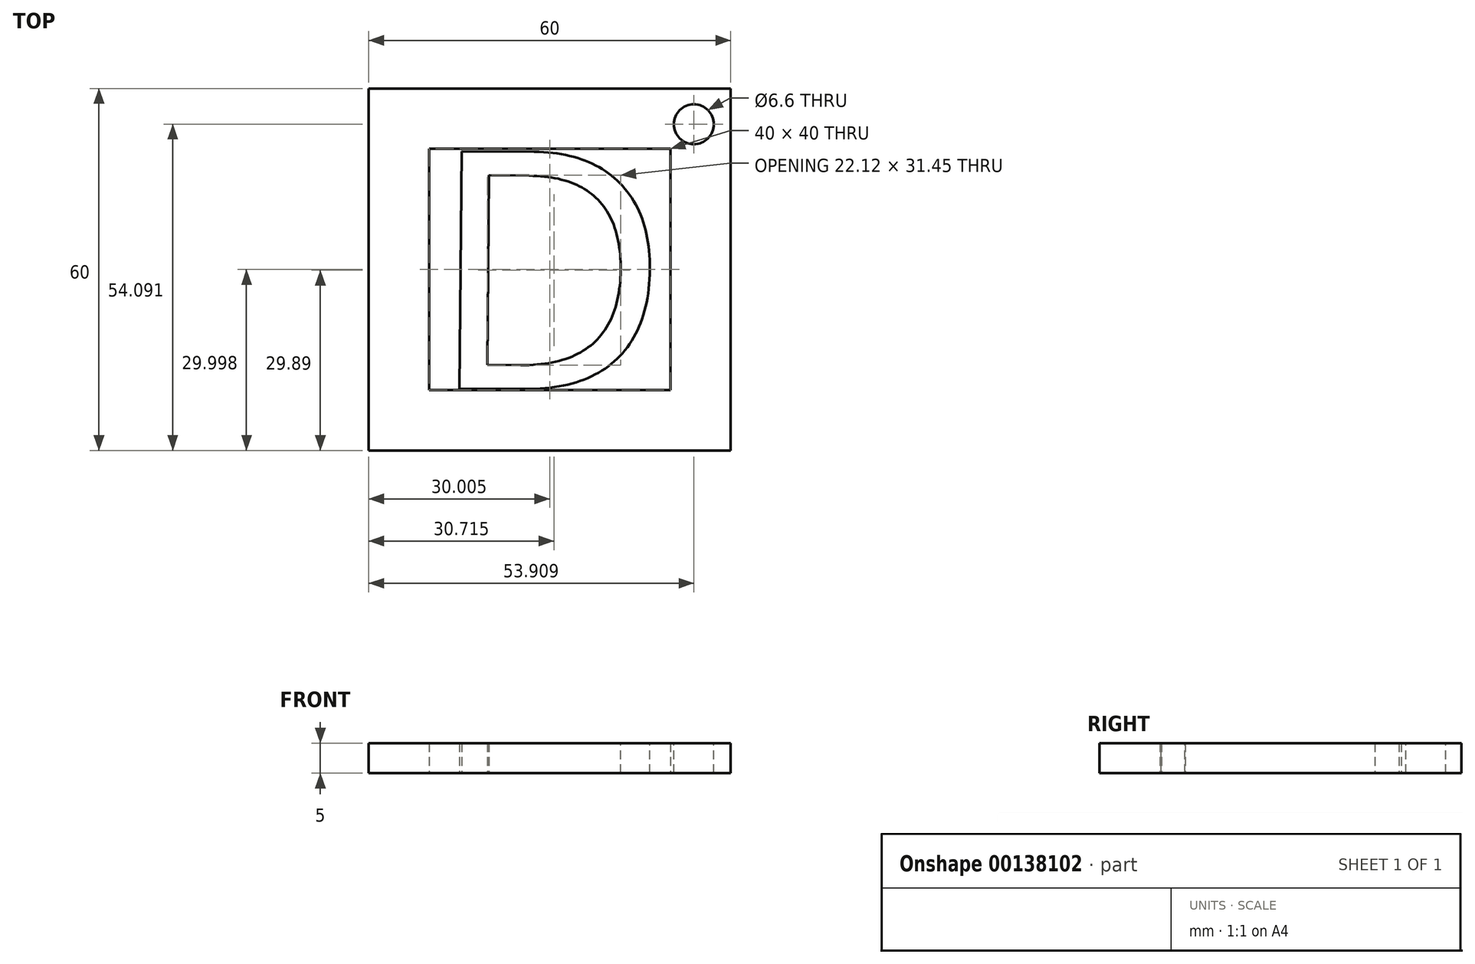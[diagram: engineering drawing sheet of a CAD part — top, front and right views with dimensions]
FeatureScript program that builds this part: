
annotation { "Feature Type Name" : "Feature", "Feature Type Description" : "" }
export const myFeature = defineFeature(function(context is Context, id is Id, definition is map)
    precondition{}
    {
        {
            var Q0;
            Q0=qCreatedBy(makeId("Top.planeOp"),FACE);
            var sketch = newSketch(context, id + "F0", { "sketchPlane" : qUnion([Q0])});
            skLineSegment(sketch, "E0.bottom", {"start": v(-26.05, 20.19) * mm, "end": v(13.95, 20.19) * mm});
            skLineSegment(sketch, "E0.top", {"start": v(-26.05, -19.81) * mm, "end": v(13.95, -19.81) * mm});
            skLineSegment(sketch, "E0.left", {"start": v(-26.05, 20.19) * mm, "end": v(-26.05, -19.81) * mm});
            skLineSegment(sketch, "E0.right", {"start": v(13.95, 20.19) * mm, "end": v(13.95, -19.81) * mm});
            skLineSegment(sketch, "E1.0", {"start": v(23.95, 30.19) * mm, "end": v(23.95, -29.81) * mm});
            skLineSegment(sketch, "E1.1", {"start": v(-36.05, 30.19) * mm, "end": v(23.95, 30.19) * mm});
            skLineSegment(sketch, "E1.2", {"start": v(-36.05, 30.19) * mm, "end": v(-36.05, -29.81) * mm});
            skLineSegment(sketch, "E1.3", {"start": v(-36.05, -29.81) * mm, "end": v(23.95, -29.81) * mm});
            skSolve(sketch);
        }
        {
            var Q0;
            Q0=makeQuery(id+"F0.imprint","IMPRINT",FACE,{"disambiguationData":[TD([[makeQuery(id+"F0.imprint","IMPRINT",EDGE,{"derivedFrom":sQuery(id+"F0.wireOp",EDGE,"E0.bottom")}),-1.0]])]});
            var sketch = newSketch(context, id + "F1", { "sketchPlane" : qUnion([Q0])});
            skLineSegment(sketch, "E2.0", {"start": v(-26.05, 20.19) * mm, "end": v(13.95, 20.19) * mm});
            skLineSegment(sketch, "E3.0", {"start": v(-26.05, 20.19) * mm, "end": v(-26.05, -19.81) * mm});
            skLineSegment(sketch, "E4.0", {"start": v(13.95, 20.19) * mm, "end": v(13.95, -19.81) * mm});
            skLineSegment(sketch, "E5.0", {"start": v(-26.05, -19.81) * mm, "end": v(13.95, -19.81) * mm});
            skText(sketch, "E6", { "text": "D", "fontName": "OpenSans-Regular.ttf"});
            const initialGuessF1  = {"E6": [-0.0264, -0.01946, 0.99996, -0.00882, 0.03965]};
            skSetInitialGuess(sketch, initialGuessF1);
            skSolve(sketch);
        }
        {
            var Q0;
            Q0=makeQuery(id+"F0.imprint","IMPRINT",FACE,{"disambiguationData":[TD([[makeQuery(id+"F0.imprint","IMPRINT",EDGE,{"derivedFrom":sQuery(id+"F0.wireOp",EDGE,"E0.bottom")}),1.0]])]});
            extrude(context, id + "F2", {"entities" : qUnion([Q0]), "depth" : 5 * mm});
        }
        {
            var Q0;
            Q0=makeQuery(id+"F1.imprint","IMPRINT",FACE,{"disambiguationData":[TD([[makeQuery(id+"F1.imprint","IMPRINT",EDGE,{"derivedFrom":sQuery(id+"F1.wireOp",EDGE,"E6.sketch_text.stroke-0")}),-1.0]])]});
            extrude(context, id + "F3", {"entities" : qUnion([Q0]), "depth" : 5 * mm});
        }
        {
            var Q0;
            Q0=makeQuery(id+"F2.opExtrude","CAP_FACE",FACE,{"disambiguationData":[OSD([sQuery(id+"F0.wireOp",EDGE,"E0.bottom"),sQuery(id+"F0.wireOp",EDGE,"E0.top"),sQuery(id+"F0.wireOp",EDGE,"E0.left"),sQuery(id+"F0.wireOp",EDGE,"E0.right"),sQuery(id+"F0.wireOp",EDGE,"E1.0"),sQuery(id+"F0.wireOp",EDGE,"E1.1"),sQuery(id+"F0.wireOp",EDGE,"E1.2"),sQuery(id+"F0.wireOp",EDGE,"E1.3")])],"isStart":false});
            var sketch = newSketch(context, id + "F4", { "sketchPlane" : qUnion([Q0])});
            skCircle(sketch, "E7", {"center": v(17.86, 24.28) * mm, "radius": 3.3 * mm});
            skSolve(sketch);
        }
        {
            var Q0;
            Q0 = qSketchRegion(id + "F4", true);
            extrude(context, id + "F5", {"entities" : qUnion([Q0]), "operationType" : NewBodyOperationType.REMOVE, "oppositeDirection" : true, "depth" : 25.4 * mm});
        }
    });
